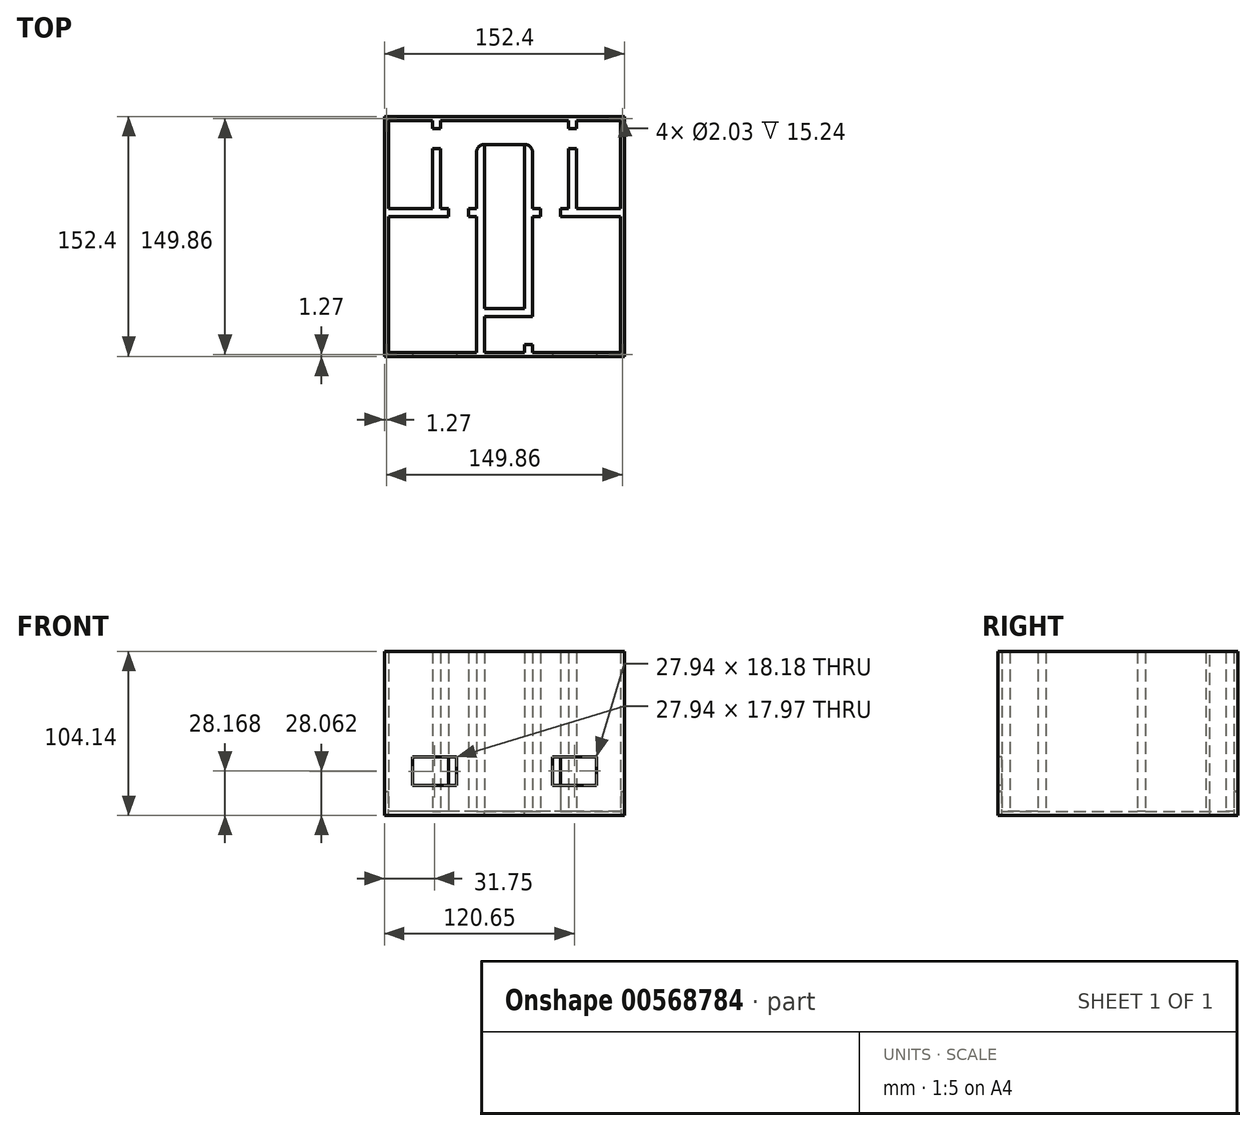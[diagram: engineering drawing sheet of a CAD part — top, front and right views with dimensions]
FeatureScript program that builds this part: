
annotation { "Feature Type Name" : "Feature", "Feature Type Description" : "" }
export const myFeature = defineFeature(function(context is Context, id is Id, definition is map)
    precondition{}
    {
        {
            var Q0;
            Q0=qCreatedBy(makeId("Top.planeOp"),FACE);
            var sketch = newSketch(context, id + "F0", { "sketchPlane" : qUnion([Q0])});
            skLineSegment(sketch, "E0.bottom", {"start": v(-76.2, 76.2) * mm, "end": v(76.2, 76.2) * mm});
            skLineSegment(sketch, "E0.top", {"start": v(-76.2, -76.2) * mm, "end": v(76.2, -76.2) * mm});
            skLineSegment(sketch, "E0.left", {"start": v(-76.2, 76.2) * mm, "end": v(-76.2, -76.2) * mm});
            skLineSegment(sketch, "E0.right", {"start": v(76.2, 76.2) * mm, "end": v(76.2, -76.2) * mm});
            skLineSegment(sketch, "E1.bottom", {"start": v(73.66, -73.66) * mm, "end": v(-73.66, -73.66) * mm});
            skLineSegment(sketch, "E1.top", {"start": v(73.66, 73.66) * mm, "end": v(-73.66, 73.66) * mm});
            skLineSegment(sketch, "E1.left", {"start": v(73.66, -73.66) * mm, "end": v(73.66, 73.66) * mm});
            skLineSegment(sketch, "E1.right", {"start": v(-73.66, -73.66) * mm, "end": v(-73.66, 73.66) * mm});
            skSolve(sketch);
        }
        {
            var Q0;
            Q0 = qSketchRegion(id + "F0", true);
            extrude(context, id + "F1", {"entities" : qUnion([Q0]), "depth" : 101.6 * mm, "offsetDistance" : 25.4 * mm});
        }
        {
            var Q0;
            Q0=makeQuery(id+"F1.opExtrude","CAP_FACE",FACE,{"disambiguationData":[OSD([sQuery(id+"F0.wireOp",EDGE,"E0.bottom"),sQuery(id+"F0.wireOp",EDGE,"E0.top"),sQuery(id+"F0.wireOp",EDGE,"E0.left"),sQuery(id+"F0.wireOp",EDGE,"E0.right"),sQuery(id+"F0.wireOp",EDGE,"E1.bottom"),sQuery(id+"F0.wireOp",EDGE,"E1.top"),sQuery(id+"F0.wireOp",EDGE,"E1.left"),sQuery(id+"F0.wireOp",EDGE,"E1.right")])],"isStart":true});
            var sketch = newSketch(context, id + "F2", { "sketchPlane" : qUnion([Q0])});
            skLineSegment(sketch, "E2.bottom", {"start": v(-76.2, -76.2) * mm, "end": v(76.2, -76.2) * mm});
            skLineSegment(sketch, "E2.top", {"start": v(-76.2, 76.2) * mm, "end": v(76.2, 76.2) * mm});
            skLineSegment(sketch, "E2.left", {"start": v(-76.2, -76.2) * mm, "end": v(-76.2, 76.2) * mm});
            skLineSegment(sketch, "E2.right", {"start": v(76.2, -76.2) * mm, "end": v(76.2, 76.2) * mm});
            skSolve(sketch);
        }
        {
            var Q0;
            Q0 = qSketchRegion(id + "F2", true);
            extrude(context, id + "F3", {"entities" : qUnion([Q0]), "operationType" : NewBodyOperationType.ADD, "depth" : 2.54 * mm, "offsetDistance" : 25.4 * mm});
        }
        {
            var Q0;
            Q0=makeQuery(id+"F3.boolean.opBoolean","MERGE",FACE,{"derivedFrom":[makeQuery(id+"F1.opExtrude","SWEPT_FACE",FACE,{"disambiguationData":[OSD([sQuery(id+"F0.wireOp",EDGE,"E0.top")])]}),makeQuery(id+"F3.opExtrude","SWEPT_FACE",FACE,{"disambiguationData":[OSD([sQuery(id+"F2.wireOp",EDGE,"E2.top")])]})]});
            var sketch = newSketch(context, id + "F4", { "sketchPlane" : qUnion([Q0])});
            skLineSegment(sketch, "E3.bottom", {"start": v(-58.42, 16.54) * mm, "end": v(-30.48, 16.54) * mm});
            skLineSegment(sketch, "E3.top", {"start": v(-58.42, 34.5) * mm, "end": v(-30.48, 34.5) * mm});
            skLineSegment(sketch, "E3.left", {"start": v(-58.42, 16.54) * mm, "end": v(-58.42, 34.5) * mm});
            skLineSegment(sketch, "E3.right", {"start": v(-30.48, 16.54) * mm, "end": v(-30.48, 34.5) * mm});
            skLineSegment(sketch, "E4.bottom", {"start": v(30.48, 16.54) * mm, "end": v(58.42, 16.54) * mm});
            skLineSegment(sketch, "E4.top", {"start": v(30.48, 34.72) * mm, "end": v(58.42, 34.72) * mm});
            skLineSegment(sketch, "E4.left", {"start": v(30.48, 16.54) * mm, "end": v(30.48, 34.72) * mm});
            skLineSegment(sketch, "E4.right", {"start": v(58.42, 16.54) * mm, "end": v(58.42, 34.72) * mm});
            skSolve(sketch);
        }
        {
            var Q0;
            Q0=makeQuery(id+"F4.imprint","IMPRINT",FACE,{"disambiguationData":[TD([[makeQuery(id+"F4.imprint","IMPRINT",EDGE,{"derivedFrom":sQuery(id+"F4.wireOp",EDGE,"E4.bottom")}),1.0]])]});
            var Q1;
            Q1=makeQuery(id+"F4.imprint","IMPRINT",FACE,{"disambiguationData":[TD([[makeQuery(id+"F4.imprint","IMPRINT",EDGE,{"derivedFrom":sQuery(id+"F4.wireOp",EDGE,"E3.bottom")}),1.0]])]});
            extrude(context, id + "F5", {"entities" : qUnion([Q0, Q1]), "operationType" : NewBodyOperationType.REMOVE, "oppositeDirection" : true, "depth" : 25.4 * mm, "offsetDistance" : 25.4 * mm});
        }
        {
            var Q0;
            Q0=makeQuery(id+"F3.opExtrude","CAP_FACE",FACE,{"disambiguationData":[OSD([sQuery(id+"F2.wireOp",EDGE,"E2.bottom"),sQuery(id+"F2.wireOp",EDGE,"E2.top"),sQuery(id+"F2.wireOp",EDGE,"E2.left"),sQuery(id+"F2.wireOp",EDGE,"E2.right")])],"isStart":true});
            var sketch = newSketch(context, id + "F6", { "sketchPlane" : qUnion([Q0])});
            skLineSegment(sketch, "E5", {"start": v(0, 0) * mm, "end": v(0, 73.66) * mm, "construction": true});
            skLineSegment(sketch, "E6", {"start": v(-73.66, 0) * mm, "end": v(73.66, 0) * mm, "construction": true});
            skLineSegment(sketch, "E7", {"start": v(-17.78, -50.8) * mm, "end": v(-17.78, 58.42) * mm});
            skLineSegment(sketch, "E8", {"start": v(17.78, -50.8) * mm, "end": v(17.78, 44.53) * mm});
            skLineSegment(sketch, "E9.bottom", {"start": v(-17.78, 58.42) * mm, "end": v(17.78, 58.42) * mm});
            skLineSegment(sketch, "E9.top", {"start": v(-17.78, -50.8) * mm, "end": v(-12.7, -50.8) * mm});
            skLineSegment(sketch, "E9.left", {"start": v(-17.78, 58.42) * mm, "end": v(-17.78, -50.8) * mm});
            skLineSegment(sketch, "E9.right", {"start": v(17.78, 58.42) * mm, "end": v(17.78, -50.8) * mm});
            skPoint(sketch, "E10.start.orphan", {"position": v(0, -73.66) * mm});
            skLineSegment(sketch, "E11.bottom", {"start": v(-12.7, 53.34) * mm, "end": v(12.7, 53.34) * mm});
            skLineSegment(sketch, "E11.left", {"start": v(-12.7, 53.34) * mm, "end": v(-12.7, -50.8) * mm});
            skLineSegment(sketch, "E11.right", {"start": v(12.7, 53.34) * mm, "end": v(12.7, -50.8) * mm});
            skLineSegment(sketch, "E12.trimOffspring", {"start": v(12.7, -50.8) * mm, "end": v(17.78, -50.8) * mm});
            skSolve(sketch);
        }
        {
            var Q0;
            {var subQ1=sQuery(id+"F6.wireOp",EDGE,"E9.bottom");Q0=makeQuery(id+"F6.imprint","IMPRINT",FACE,{"disambiguationData":[TD([[makeQuery(id+"F6.imprint","IMPRINT",EDGE,{"derivedFrom":subQ1}),-1.0]])]});}
            extrude(context, id + "F7", {"entities" : qUnion([Q0]), "operationType" : NewBodyOperationType.ADD, "depth" : 101.6 * mm, "offsetDistance" : 25.4 * mm});
        }
        {
            var Q0;
            Q0=makeQuery(id+"F3.opExtrude","CAP_FACE",FACE,{"disambiguationData":[OSD([sQuery(id+"F2.wireOp",EDGE,"E2.bottom"),sQuery(id+"F2.wireOp",EDGE,"E2.top"),sQuery(id+"F2.wireOp",EDGE,"E2.left"),sQuery(id+"F2.wireOp",EDGE,"E2.right")])],"isStart":true});
            var sketch = newSketch(context, id + "F8", { "sketchPlane" : qUnion([Q0])});
            skLineSegment(sketch, "E13.bottom", {"start": v(12.7, -50.8) * mm, "end": v(-12.7, -50.8) * mm});
            skLineSegment(sketch, "E13.top", {"start": v(12.7, -45.72) * mm, "end": v(-12.7, -45.72) * mm});
            skLineSegment(sketch, "E13.left", {"start": v(12.7, -50.8) * mm, "end": v(12.7, -45.72) * mm});
            skLineSegment(sketch, "E13.right", {"start": v(-12.7, -50.8) * mm, "end": v(-12.7, -45.72) * mm});
            skSolve(sketch);
        }
        {
            var Q0;
            Q0 = qSketchRegion(id + "F8", true);
            extrude(context, id + "F9", {"entities" : qUnion([Q0]), "operationType" : NewBodyOperationType.ADD, "depth" : 101.6 * mm, "offsetDistance" : 25.4 * mm});
        }
        {
            var Q0;
            Q0=makeQuery(id+"F9.boolean.opBoolean","MERGE",FACE,{"derivedFrom":[makeQuery(id+"F7.opExtrude","CAP_FACE",FACE,{"disambiguationData":[OSD([sQuery(id+"F6.wireOp",EDGE,"E9.bottom"),sQuery(id+"F6.wireOp",EDGE,"E9.top"),sQuery(id+"F6.wireOp",EDGE,"E9.left"),sQuery(id+"F6.wireOp",EDGE,"E9.right"),sQuery(id+"F6.wireOp",EDGE,"E11.bottom"),sQuery(id+"F6.wireOp",EDGE,"E11.left"),sQuery(id+"F6.wireOp",EDGE,"E11.right"),sQuery(id+"F6.wireOp",EDGE,"E12.trimOffspring")])],"isStart":false}),makeQuery(id+"F9.opExtrude","CAP_FACE",FACE,{"disambiguationData":[OSD([sQuery(id+"F8.wireOp",EDGE,"E13.bottom"),sQuery(id+"F8.wireOp",EDGE,"E13.top"),sQuery(id+"F8.wireOp",EDGE,"E13.left"),sQuery(id+"F8.wireOp",EDGE,"E13.right")])],"isStart":false})]});
            var sketch = newSketch(context, id + "F10", { "sketchPlane" : qUnion([Q0])});
            skLineSegment(sketch, "E14.bottom", {"start": v(-12.7, 53.34) * mm, "end": v(12.7, 53.34) * mm});
            skLineSegment(sketch, "E14.top", {"start": v(-12.7, 58.42) * mm, "end": v(12.7, 58.42) * mm});
            skLineSegment(sketch, "E14.left", {"start": v(-12.7, 53.34) * mm, "end": v(-12.7, 58.42) * mm});
            skLineSegment(sketch, "E14.right", {"start": v(12.7, 53.34) * mm, "end": v(12.7, 58.42) * mm});
            skSolve(sketch);
        }
        {
            var Q0;
            Q0 = qSketchRegion(id + "F10", true);
            extrude(context, id + "F11", {"entities" : qUnion([Q0]), "operationType" : NewBodyOperationType.REMOVE, "oppositeDirection" : true, "depth" : 101.6 * mm, "offsetDistance" : 25.4 * mm});
        }
        {
            var Q0;
            {var subQ0=makeQuery(id+"F3.opExtrude","CAP_FACE",FACE,{"disambiguationData":[OSD([sQuery(id+"F2.wireOp",EDGE,"E2.bottom"),sQuery(id+"F2.wireOp",EDGE,"E2.top"),sQuery(id+"F2.wireOp",EDGE,"E2.left"),sQuery(id+"F2.wireOp",EDGE,"E2.right")])],"isStart":true});Q0=makeQuery(id+"F11.boolean.opBoolean","MERGE",FACE,{"derivedFrom":[makeQuery(id+"F9.boolean.opBoolean","SPLIT",FACE,{"disambiguationData":[TD([makeQuery(id+"F1.opExtrude","SWEPT_FACE",FACE,{"disambiguationData":[OSD([sQuery(id+"F0.wireOp",EDGE,"E1.bottom")])]})])],"derivedFrom":subQ0}),makeQuery(id+"F9.boolean.opBoolean","SPLIT",FACE,{"disambiguationData":[TD([makeQuery(id+"F7.opExtrude","SWEPT_FACE",FACE,{"disambiguationData":[OSD([sQuery(id+"F6.wireOp",EDGE,"E11.bottom")])]})])],"derivedFrom":subQ0}),makeQuery(id+"F11.opExtrude","CAP_FACE",FACE,{"disambiguationData":[OSD([sQuery(id+"F10.wireOp",EDGE,"E14.bottom"),sQuery(id+"F10.wireOp",EDGE,"E14.top"),sQuery(id+"F10.wireOp",EDGE,"E14.left"),sQuery(id+"F10.wireOp",EDGE,"E14.right")])],"isStart":false})]});}
            var sketch = newSketch(context, id + "F12", { "sketchPlane" : qUnion([Q0])});
            skLineSegment(sketch, "E15.bottom", {"start": v(-17.78, 17.47) * mm, "end": v(-22.86, 17.47) * mm});
            skLineSegment(sketch, "E15.top", {"start": v(-17.78, 12.4) * mm, "end": v(-22.86, 12.4) * mm});
            skLineSegment(sketch, "E15.left", {"start": v(-17.78, 17.47) * mm, "end": v(-17.78, 12.4) * mm});
            skLineSegment(sketch, "E15.right", {"start": v(-22.86, 17.47) * mm, "end": v(-22.86, 12.4) * mm});
            skSolve(sketch);
        }
        {
            var Q0;
            Q0 = qSketchRegion(id + "F12", true);
            extrude(context, id + "F13", {"entities" : qUnion([Q0]), "operationType" : NewBodyOperationType.ADD, "depth" : 101.6 * mm, "offsetDistance" : 25.4 * mm});
        }
        {
            var Q0;
            {var subQ0=makeQuery(id+"F3.opExtrude","CAP_FACE",FACE,{"disambiguationData":[OSD([sQuery(id+"F2.wireOp",EDGE,"E2.bottom"),sQuery(id+"F2.wireOp",EDGE,"E2.top"),sQuery(id+"F2.wireOp",EDGE,"E2.left"),sQuery(id+"F2.wireOp",EDGE,"E2.right")])],"isStart":true});Q0=makeQuery(id+"F11.boolean.opBoolean","MERGE",FACE,{"derivedFrom":[makeQuery(id+"F9.boolean.opBoolean","SPLIT",FACE,{"disambiguationData":[TD([makeQuery(id+"F1.opExtrude","SWEPT_FACE",FACE,{"disambiguationData":[OSD([sQuery(id+"F0.wireOp",EDGE,"E1.bottom")])]})])],"derivedFrom":subQ0}),makeQuery(id+"F9.boolean.opBoolean","SPLIT",FACE,{"disambiguationData":[TD([makeQuery(id+"F7.opExtrude","SWEPT_FACE",FACE,{"disambiguationData":[OSD([sQuery(id+"F6.wireOp",EDGE,"E11.bottom")])]})])],"derivedFrom":subQ0}),makeQuery(id+"F11.opExtrude","CAP_FACE",FACE,{"disambiguationData":[OSD([sQuery(id+"F10.wireOp",EDGE,"E14.bottom"),sQuery(id+"F10.wireOp",EDGE,"E14.top"),sQuery(id+"F10.wireOp",EDGE,"E14.left"),sQuery(id+"F10.wireOp",EDGE,"E14.right")])],"isStart":false})]});}
            var sketch = newSketch(context, id + "F14", { "sketchPlane" : qUnion([Q0])});
            skLineSegment(sketch, "E16.bottom", {"start": v(-35.56, 17.47) * mm, "end": v(-73.66, 17.47) * mm});
            skLineSegment(sketch, "E16.top", {"start": v(-35.56, 12.4) * mm, "end": v(-73.66, 12.4) * mm});
            skLineSegment(sketch, "E16.left", {"start": v(-35.56, 17.47) * mm, "end": v(-35.56, 12.4) * mm});
            skLineSegment(sketch, "E16.right", {"start": v(-73.66, 17.47) * mm, "end": v(-73.66, 12.4) * mm});
            skSolve(sketch);
        }
        {
            var Q0;
            Q0=makeQuery(id+"F14.imprint","IMPRINT",FACE,{"disambiguationData":[TD([[makeQuery(id+"F14.imprint","IMPRINT",EDGE,{"derivedFrom":sQuery(id+"F14.wireOp",EDGE,"E16.bottom")}),1.0]])]});
            extrude(context, id + "F15", {"entities" : qUnion([Q0]), "operationType" : NewBodyOperationType.ADD, "depth" : 101.6 * mm, "offsetDistance" : 25.4 * mm});
        }
        {
            var Q0;
            {var subQ0=makeQuery(id+"F3.opExtrude","CAP_FACE",FACE,{"disambiguationData":[OSD([sQuery(id+"F2.wireOp",EDGE,"E2.bottom"),sQuery(id+"F2.wireOp",EDGE,"E2.top"),sQuery(id+"F2.wireOp",EDGE,"E2.left"),sQuery(id+"F2.wireOp",EDGE,"E2.right")])],"isStart":true});Q0=makeQuery(id+"F11.boolean.opBoolean","MERGE",FACE,{"derivedFrom":[makeQuery(id+"F9.boolean.opBoolean","SPLIT",FACE,{"disambiguationData":[TD([makeQuery(id+"F1.opExtrude","SWEPT_FACE",FACE,{"disambiguationData":[OSD([sQuery(id+"F0.wireOp",EDGE,"E1.bottom")])]})])],"derivedFrom":subQ0}),makeQuery(id+"F9.boolean.opBoolean","SPLIT",FACE,{"disambiguationData":[TD([makeQuery(id+"F7.opExtrude","SWEPT_FACE",FACE,{"disambiguationData":[OSD([sQuery(id+"F6.wireOp",EDGE,"E11.bottom")])]})])],"derivedFrom":subQ0}),makeQuery(id+"F11.opExtrude","CAP_FACE",FACE,{"disambiguationData":[OSD([sQuery(id+"F10.wireOp",EDGE,"E14.bottom"),sQuery(id+"F10.wireOp",EDGE,"E14.top"),sQuery(id+"F10.wireOp",EDGE,"E14.left"),sQuery(id+"F10.wireOp",EDGE,"E14.right")])],"isStart":false})]});}
            var sketch = newSketch(context, id + "F16", { "sketchPlane" : qUnion([Q0])});
            skLineSegment(sketch, "E17.bottom", {"start": v(-45.72, 17.47) * mm, "end": v(-40.64, 17.47) * mm});
            skLineSegment(sketch, "E17.top", {"start": v(-45.72, 55.88) * mm, "end": v(-40.64, 55.88) * mm});
            skLineSegment(sketch, "E17.left", {"start": v(-45.72, 17.47) * mm, "end": v(-45.72, 55.88) * mm});
            skLineSegment(sketch, "E17.right", {"start": v(-40.64, 17.47) * mm, "end": v(-40.64, 55.88) * mm});
            skLineSegment(sketch, "E18.bottom", {"start": v(-45.72, 73.66) * mm, "end": v(-40.64, 73.66) * mm});
            skLineSegment(sketch, "E18.top", {"start": v(-45.72, 68.58) * mm, "end": v(-40.64, 68.58) * mm});
            skLineSegment(sketch, "E18.left", {"start": v(-45.72, 73.66) * mm, "end": v(-45.72, 68.58) * mm});
            skLineSegment(sketch, "E18.right", {"start": v(-40.64, 73.66) * mm, "end": v(-40.64, 68.58) * mm});
            skLineSegment(sketch, "E19", {"start": v(0, 73.66) * mm, "end": v(0, -73.66) * mm, "construction": true});
            skLineSegment(sketch, "E20.MirrorCS", {"start": v(45.72, 73.66) * mm, "end": v(45.72, 68.58) * mm});
            skLineSegment(sketch, "E21.MirrorCS", {"start": v(45.72, 68.58) * mm, "end": v(40.64, 68.58) * mm});
            skLineSegment(sketch, "E22.MirrorCS", {"start": v(40.64, 73.66) * mm, "end": v(40.64, 68.58) * mm});
            skLineSegment(sketch, "E23.MirrorCS", {"start": v(45.72, 73.66) * mm, "end": v(40.64, 73.66) * mm});
            skLineSegment(sketch, "E24.MirrorCS", {"start": v(45.72, 55.88) * mm, "end": v(40.64, 55.88) * mm});
            skLineSegment(sketch, "E25.MirrorCS", {"start": v(45.72, 17.47) * mm, "end": v(45.72, 55.88) * mm});
            skLineSegment(sketch, "E26.MirrorCS", {"start": v(40.64, 17.47) * mm, "end": v(40.64, 55.88) * mm});
            skLineSegment(sketch, "E27.MirrorCS", {"start": v(45.72, 17.47) * mm, "end": v(40.64, 17.47) * mm});
            skSolve(sketch);
        }
        {
            var Q0;
            Q0 = qSketchRegion(id + "F16", true);
            extrude(context, id + "F17", {"entities" : qUnion([Q0]), "operationType" : NewBodyOperationType.ADD, "depth" : 101.6 * mm, "offsetDistance" : 25.4 * mm});
        }
        {
            var Q0;
            {var subQ0=makeQuery(id+"F3.opExtrude","CAP_FACE",FACE,{"disambiguationData":[OSD([sQuery(id+"F2.wireOp",EDGE,"E2.bottom"),sQuery(id+"F2.wireOp",EDGE,"E2.top"),sQuery(id+"F2.wireOp",EDGE,"E2.left"),sQuery(id+"F2.wireOp",EDGE,"E2.right")])],"isStart":true});Q0=makeQuery(id+"F11.boolean.opBoolean","MERGE",FACE,{"derivedFrom":[makeQuery(id+"F9.boolean.opBoolean","SPLIT",FACE,{"disambiguationData":[TD([makeQuery(id+"F1.opExtrude","SWEPT_FACE",FACE,{"disambiguationData":[OSD([sQuery(id+"F0.wireOp",EDGE,"E1.bottom")])]})])],"derivedFrom":subQ0}),makeQuery(id+"F9.boolean.opBoolean","SPLIT",FACE,{"disambiguationData":[TD([makeQuery(id+"F7.opExtrude","SWEPT_FACE",FACE,{"disambiguationData":[OSD([sQuery(id+"F6.wireOp",EDGE,"E11.bottom")])]})])],"derivedFrom":subQ0}),makeQuery(id+"F11.opExtrude","CAP_FACE",FACE,{"disambiguationData":[OSD([sQuery(id+"F10.wireOp",EDGE,"E14.bottom"),sQuery(id+"F10.wireOp",EDGE,"E14.top"),sQuery(id+"F10.wireOp",EDGE,"E14.left"),sQuery(id+"F10.wireOp",EDGE,"E14.right")])],"isStart":false})]});}
            var sketch = newSketch(context, id + "F18", { "sketchPlane" : qUnion([Q0])});
            skLineSegment(sketch, "E28.bottom", {"start": v(-12.7, 58.42) * mm, "end": v(12.7, 58.42) * mm});
            skLineSegment(sketch, "E28.top", {"start": v(-12.7, -45.72) * mm, "end": v(12.7, -45.72) * mm});
            skLineSegment(sketch, "E28.left", {"start": v(-12.7, 58.42) * mm, "end": v(-12.7, -45.72) * mm});
            skLineSegment(sketch, "E28.right", {"start": v(12.7, 58.42) * mm, "end": v(12.7, -45.72) * mm});
            skSolve(sketch);
        }
        {
            var Q0;
            Q0 = qSketchRegion(id + "F18", true);
            extrude(context, id + "F19", {"entities" : qUnion([Q0]), "operationType" : NewBodyOperationType.REMOVE, "oppositeDirection" : true, "depth" : 25.4 * mm, "offsetDistance" : 25.4 * mm});
        }
        {
            var Q0;
            Q0=makeQuery(id+"F7.opExtrude","SWEPT_EDGE",EDGE,{"disambiguationData":[OSD([sQuery(id+"F6.wireOp",EDGE,"E9.bottom"),sQuery(id+"F6.wireOp",EDGE,"E9.left")])]});
            var Q1;
            Q1=makeQuery(id+"F7.opExtrude","SWEPT_EDGE",EDGE,{"disambiguationData":[OSD([sQuery(id+"F6.wireOp",EDGE,"E9.bottom"),sQuery(id+"F6.wireOp",EDGE,"E9.right")])]});
            fillet(context, id + "F20", {"entities" : qUnion([Q0, Q1]), "radius" : 5.08 * mm, "tangentPropagation" : true, "allowEdgeOverflow" : false});
        }
        {
            var Q0;
            {var subQ0=makeQuery(id+"F3.opExtrude","CAP_FACE",FACE,{"disambiguationData":[OSD([sQuery(id+"F2.wireOp",EDGE,"E2.bottom"),sQuery(id+"F2.wireOp",EDGE,"E2.top"),sQuery(id+"F2.wireOp",EDGE,"E2.left"),sQuery(id+"F2.wireOp",EDGE,"E2.right")])],"isStart":true});Q0=makeQuery(id+"F11.boolean.opBoolean","MERGE",FACE,{"derivedFrom":[makeQuery(id+"F9.boolean.opBoolean","SPLIT",FACE,{"disambiguationData":[TD([makeQuery(id+"F1.opExtrude","SWEPT_FACE",FACE,{"disambiguationData":[OSD([sQuery(id+"F0.wireOp",EDGE,"E1.bottom")])]})])],"derivedFrom":subQ0}),makeQuery(id+"F9.boolean.opBoolean","SPLIT",FACE,{"disambiguationData":[TD([makeQuery(id+"F7.opExtrude","SWEPT_FACE",FACE,{"disambiguationData":[OSD([sQuery(id+"F6.wireOp",EDGE,"E11.bottom")])]})])],"derivedFrom":subQ0}),makeQuery(id+"F11.opExtrude","CAP_FACE",FACE,{"disambiguationData":[OSD([sQuery(id+"F10.wireOp",EDGE,"E14.bottom"),sQuery(id+"F10.wireOp",EDGE,"E14.top"),sQuery(id+"F10.wireOp",EDGE,"E14.left"),sQuery(id+"F10.wireOp",EDGE,"E14.right")])],"isStart":false})]});}
            var sketch = newSketch(context, id + "F21", { "sketchPlane" : qUnion([Q0])});
            skLineSegment(sketch, "E29.bottom", {"start": v(17.78, 17.47) * mm, "end": v(22.86, 17.47) * mm});
            skLineSegment(sketch, "E29.top", {"start": v(17.78, 12.4) * mm, "end": v(22.86, 12.4) * mm});
            skLineSegment(sketch, "E29.left", {"start": v(17.78, 17.47) * mm, "end": v(17.78, 12.4) * mm});
            skLineSegment(sketch, "E29.right", {"start": v(22.86, 17.47) * mm, "end": v(22.86, 12.4) * mm});
            skLineSegment(sketch, "E30.bottom", {"start": v(35.56, 17.47) * mm, "end": v(73.66, 17.47) * mm});
            skLineSegment(sketch, "E30.top", {"start": v(35.56, 12.4) * mm, "end": v(73.66, 12.4) * mm});
            skLineSegment(sketch, "E30.left", {"start": v(35.56, 17.47) * mm, "end": v(35.56, 12.4) * mm});
            skLineSegment(sketch, "E30.right", {"start": v(73.66, 17.47) * mm, "end": v(73.66, 12.4) * mm});
            skLineSegment(sketch, "E31.bottom", {"start": v(-17.78, -50.8) * mm, "end": v(-12.7, -50.8) * mm});
            skLineSegment(sketch, "E31.top", {"start": v(-17.78, -73.66) * mm, "end": v(-12.7, -73.66) * mm});
            skLineSegment(sketch, "E31.left", {"start": v(-17.78, -50.8) * mm, "end": v(-17.78, -73.66) * mm});
            skLineSegment(sketch, "E31.right", {"start": v(-12.7, -50.8) * mm, "end": v(-12.7, -73.66) * mm});
            skLineSegment(sketch, "E32.bottom", {"start": v(17.78, -73.66) * mm, "end": v(12.7, -73.66) * mm});
            skLineSegment(sketch, "E32.top", {"start": v(17.78, -68.58) * mm, "end": v(12.7, -68.58) * mm});
            skLineSegment(sketch, "E32.left", {"start": v(17.78, -73.66) * mm, "end": v(17.78, -68.58) * mm});
            skLineSegment(sketch, "E32.right", {"start": v(12.7, -73.66) * mm, "end": v(12.7, -68.58) * mm});
            skSolve(sketch);
        }
        {
            var Q0;
            Q0 = qSketchRegion(id + "F21", true);
            extrude(context, id + "F22", {"entities" : qUnion([Q0]), "operationType" : NewBodyOperationType.ADD, "depth" : 101.6 * mm, "offsetDistance" : 25.4 * mm});
        }
        {
            var Q0;
            Q0=makeQuery(id+"F3.opExtrude","CAP_FACE",FACE,{"disambiguationData":[OSD([sQuery(id+"F2.wireOp",EDGE,"E2.bottom"),sQuery(id+"F2.wireOp",EDGE,"E2.top"),sQuery(id+"F2.wireOp",EDGE,"E2.left"),sQuery(id+"F2.wireOp",EDGE,"E2.right")])],"isStart":false});
            var sketch = newSketch(context, id + "F23", { "sketchPlane" : qUnion([Q0])});
            skCircle(sketch, "E33", {"center": v(-74.93, 74.93) * mm, "radius": 1.02 * mm});
            skCircle(sketch, "E34", {"center": v(74.93, 74.93) * mm, "radius": 1.02 * mm});
            skCircle(sketch, "E35", {"center": v(-74.93, -74.93) * mm, "radius": 1.02 * mm});
            skCircle(sketch, "E36", {"center": v(74.93, -74.93) * mm, "radius": 1.02 * mm});
            skSolve(sketch);
        }
        {
            var Q0;
            Q0 = qSketchRegion(id + "F23", true);
            extrude(context, id + "F24", {"entities" : qUnion([Q0]), "operationType" : NewBodyOperationType.REMOVE, "oppositeDirection" : true, "depth" : 15.24 * mm, "offsetDistance" : 25.4 * mm});
        }
    });
